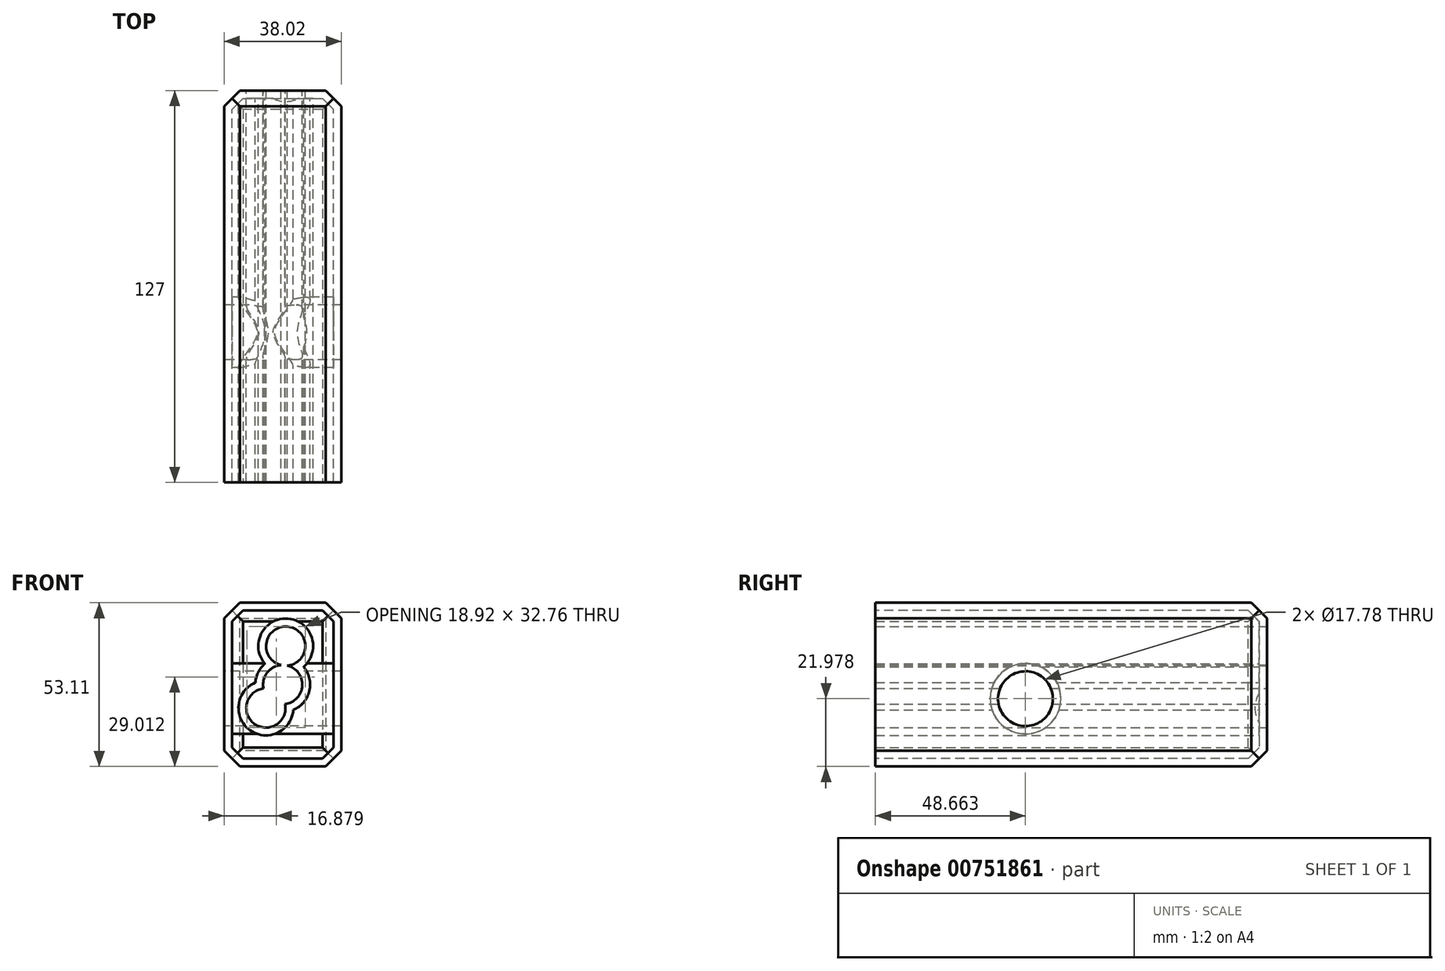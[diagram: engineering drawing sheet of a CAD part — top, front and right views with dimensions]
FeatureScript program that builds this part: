
annotation { "Feature Type Name" : "Feature", "Feature Type Description" : "" }
export const myFeature = defineFeature(function(context is Context, id is Id, definition is map)
    precondition{}
    {
        {
            var Q0;
            Q0=qCreatedBy(makeId("Front.planeOp"),FACE);
            var sketch = newSketch(context, id + "F0", { "sketchPlane" : qUnion([Q0])});
            skLineSegment(sketch, "E0.bottom", {"start": v(0, -19.31) * mm, "end": v(0, -19.31) * mm});
            skLineSegment(sketch, "E0.top", {"start": v(0, 19.31) * mm, "end": v(0, 19.31) * mm});
            skLineSegment(sketch, "E0.left", {"start": v(0, -19.31) * mm, "end": v(0, 19.31) * mm});
            skLineSegment(sketch, "E0.right", {"start": v(0, -19.31) * mm, "end": v(0, 19.31) * mm});
            skPoint(sketch, "E0.middle", {"position": v(0, 0) * mm});
            skLineSegment(sketch, "E1.bottom", {"start": v(22.33, 13.58) * mm, "end": v(60.35, 13.58) * mm});
            skLineSegment(sketch, "E1.top", {"start": v(22.33, -39.53) * mm, "end": v(60.35, -39.53) * mm});
            skLineSegment(sketch, "E1.left", {"start": v(22.33, 13.58) * mm, "end": v(22.33, -39.53) * mm});
            skLineSegment(sketch, "E1.right", {"start": v(60.35, 13.58) * mm, "end": v(60.35, -39.53) * mm});
            skPoint(sketch, "E1.middle", {"position": v(41.34, -12.97) * mm});
            skPoint(sketch, "E2", {"position": v(41.34, -39.53) * mm});
            skPoint(sketch, "E3", {"position": v(35.9, -20.55) * mm});
            skPoint(sketch, "E4", {"position": v(22.33, -0.99) * mm});
            skPoint(sketch, "E5", {"position": v(42.32, -0.47) * mm});
            skSolve(sketch);
        }
        {
            var Q0;
            Q0=makeQuery(id+"F0.imprint","IMPRINT",FACE,{"disambiguationData":[TD([[makeQuery(id+"F0.imprint","IMPRINT",EDGE,{"derivedFrom":sQuery(id+"F0.wireOp",EDGE,"E1.bottom")}),-1.0]])]});
            extrude(context, id + "F1", {"entities" : qUnion([Q0]), "depth" : 127 * mm, "offsetDistance" : 25.4 * mm});
        }
        {
            var Q0;
            Q0=sQuery(id+"F0.wireOp",VERTEX,"E3");
            var Q1;
            Q1=sQuery(id+"F0.wireOp",VERTEX,"E5");
            var Q2;
            Q2=sQuery(id+"F0.wireOp",VERTEX,"E1.middle");
            var Q3;
            Q3=makeQuery(id+"F1.opExtrude","SWEPT_BODY",BODY,{"disambiguationData":[OSD([sQuery(id+"F0.wireOp",EDGE,"E1.bottom"),sQuery(id+"F0.wireOp",EDGE,"E1.top"),sQuery(id+"F0.wireOp",EDGE,"E1.left"),sQuery(id+"F0.wireOp",EDGE,"E1.right")])]});
            hole(context, id + "F2", {"style" : HoleStyle.SIMPLE, "endStyle" : HoleEndStyle.THROUGH, "oppositeDirection" : true, "holeDiameter" : 12.7 * mm, "majorDiameter" : 6.35 * mm, "isTappedThrough" : true, "tappedDepth" : 12.7 * mm, "tapClearance" : 3, "locations" : qUnion([Q0, Q1, Q2]), "scope" : qUnion([Q3])});
        }
        {
            var Q0;
            Q0=qCreatedBy(makeId("Right.planeOp"),FACE);
            var sketch = newSketch(context, id + "F3", { "sketchPlane" : qUnion([Q0])});
            skPoint(sketch, "E6", {"position": v(-245.05, -13.26) * mm});
            skPoint(sketch, "E7", {"position": v(-78.34, -17.55) * mm});
            skSolve(sketch);
        }
        {
            var Q0;
            Q0=sQuery(id+"F3.wireOp",VERTEX,"E7");
            var Q1;
            Q1=sQuery(id+"F3.wireOp",VERTEX,"E6");
            var Q2;
            Q2=makeQuery(id+"F1.opExtrude","SWEPT_BODY",BODY,{"disambiguationData":[OSD([sQuery(id+"F0.wireOp",EDGE,"E1.bottom"),sQuery(id+"F0.wireOp",EDGE,"E1.top"),sQuery(id+"F0.wireOp",EDGE,"E1.left"),sQuery(id+"F0.wireOp",EDGE,"E1.right")])]});
            hole(context, id + "F4", {"style" : HoleStyle.SIMPLE, "endStyle" : HoleEndStyle.THROUGH, "oppositeDirection" : true, "holeDiameter" : 17.78 * mm, "majorDiameter" : 6.35 * mm, "isTappedThrough" : true, "tappedDepth" : 12.7 * mm, "tapClearance" : 3, "locations" : qUnion([Q0, Q1]), "scope" : qUnion([Q2])});
        }
        {
            var Q0;
            Q0=makeQuery(id+"F1.opExtrude","SWEPT_EDGE",EDGE,{"disambiguationData":[OSD([sQuery(id+"F0.wireOp",EDGE,"E1.bottom"),sQuery(id+"F0.wireOp",EDGE,"E1.right")])]});
            var Q1;
            Q1=makeQuery(id+"F1.opExtrude","SWEPT_EDGE",EDGE,{"disambiguationData":[OSD([sQuery(id+"F0.wireOp",EDGE,"E1.bottom"),sQuery(id+"F0.wireOp",EDGE,"E1.left")])]});
            var Q2;
            Q2=makeQuery(id+"F1.opExtrude","SWEPT_EDGE",EDGE,{"disambiguationData":[OSD([sQuery(id+"F0.wireOp",EDGE,"E1.top"),sQuery(id+"F0.wireOp",EDGE,"E1.right")])]});
            var Q3;
            Q3=makeQuery(id+"F1.opExtrude","SWEPT_EDGE",EDGE,{"disambiguationData":[OSD([sQuery(id+"F0.wireOp",EDGE,"E1.top"),sQuery(id+"F0.wireOp",EDGE,"E1.left")])]});
            chamfer(context, id + "F5", {"entities" : qUnion([Q0, Q1, Q2, Q3]), "width" : 5.08 * mm, "tangentPropagation" : true});
        }
        {
            var Q0;
            Q0=makeQuery(id+"F1.opExtrude","CAP_EDGE",EDGE,{"disambiguationData":[OSD([sQuery(id+"F0.wireOp",EDGE,"E1.left")])],"isStart":true});
            var Q1;
            Q1=makeQuery(id+"F1.opExtrude","CAP_EDGE",EDGE,{"disambiguationData":[OSD([sQuery(id+"F0.wireOp",EDGE,"E1.top")])],"isStart":true});
            var Q2;
            Q2=makeQuery(id+"F1.opExtrude","CAP_EDGE",EDGE,{"disambiguationData":[OSD([sQuery(id+"F0.wireOp",EDGE,"E1.right")])],"isStart":true});
            var Q3;
            Q3=makeQuery(id+"F1.opExtrude","CAP_EDGE",EDGE,{"disambiguationData":[OSD([sQuery(id+"F0.wireOp",EDGE,"E1.bottom")])],"isStart":true});
            chamfer(context, id + "F6", {"entities" : qUnion([Q0, Q1, Q2, Q3]), "width" : 5.08 * mm, "tangentPropagation" : true});
        }
        {
            var Q0;
            Q0=makeQuery(id+"F1.opExtrude","CAP_FACE",FACE,{"disambiguationData":[OSD([sQuery(id+"F0.wireOp",EDGE,"E1.bottom"),sQuery(id+"F0.wireOp",EDGE,"E1.top"),sQuery(id+"F0.wireOp",EDGE,"E1.left"),sQuery(id+"F0.wireOp",EDGE,"E1.right")])],"isStart":false});
            shell(context, id + "F7", {"entities" : qUnion([Q0]), "thickness" : 2.54 * mm});
        }
    });
